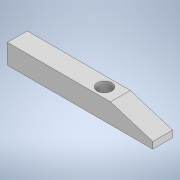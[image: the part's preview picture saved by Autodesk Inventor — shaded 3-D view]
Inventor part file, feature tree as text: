
AUTODESK INVENTOR PART (.ipt)
format: ipt  version: 2021 (Build 250183000, 183)  size: 113,152 bytes
history: native  units: mm
features: sketch x4, hole x2, other x1, extrude x1, chamfer x1
ambient origin geometry x8: Origin, YZ Plane, XZ Plane, XY Plane, X Axis, Y Axis, Z Axis, Center Point
bodies: Body1 (feature_tree)
feature tree (9):
  other  "Sólido1"
  extrude  "Extrusão1"  Depth=15.0mm
  chamfer  "Chanfro1"  Distance=15.0mm
  hole  "Furo1"  [1 undecoded]
  sketch  "Esboço3"  dims[d8=13.0mm]
  hole  "Furo2"  [1 undecoded]
  sketch  "Esboço1"  dims[d0=110.0mm d1=15.0mm d2=15.0mm d3=0.0mm]
  sketch  "Esboço2"  dims[d4=10.0mm d5=32.0mm d6=45.0deg d7=7.5mm]
  sketch  "Esboço4"  dims[d9=8.0mm d10=6.0mm d11=4.0mm d12=2.0mm d13=90.0deg d14=10.4mm d15=20.594885mm d17=53.0mm d18=11.0mm d19=6.0mm d20=4.0mm d21=2.0mm d22=90.0deg d23=10.4mm d24=20.594885mm]
note: 2 required parameter values undecoded (feature->parameter linkage not recoverable at this tier; creation-order binding heuristic only, values carry confidence <= 0.55)
